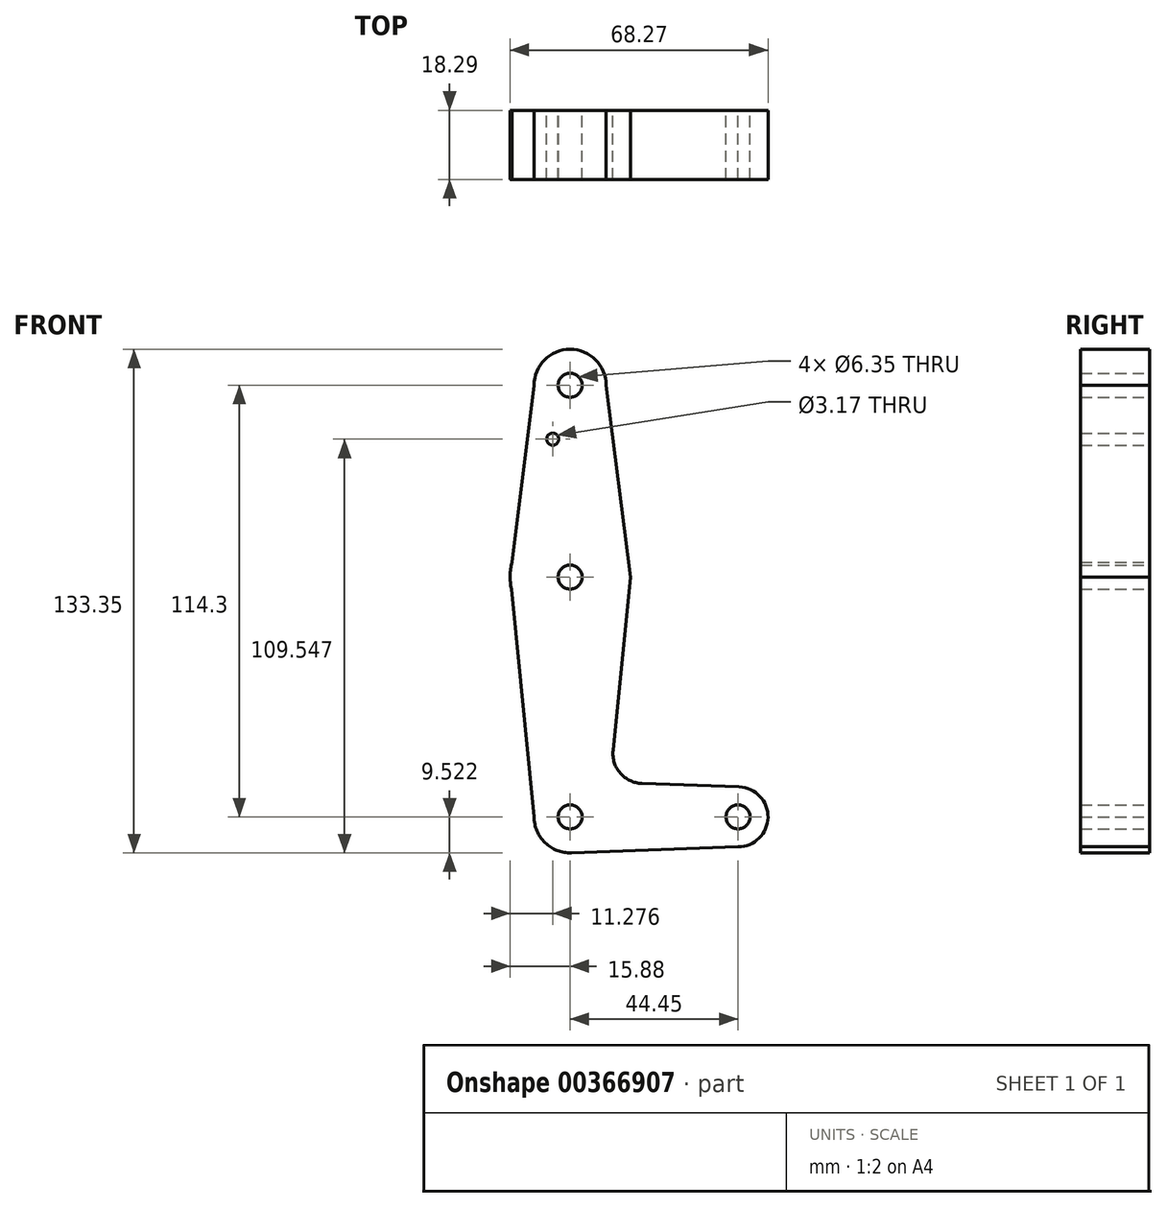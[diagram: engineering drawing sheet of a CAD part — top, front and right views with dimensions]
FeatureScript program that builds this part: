
annotation { "Feature Type Name" : "Feature", "Feature Type Description" : "" }
export const myFeature = defineFeature(function(context is Context, id is Id, definition is map)
    precondition{}
    {
        {
            var Q0;
            Q0=qCreatedBy(makeId("Front.planeOp"),FACE);
            var sketch = newSketch(context, id + "F0", { "sketchPlane" : qUnion([Q0])});
            skCircle(sketch, "E0", {"center": v(0, 88.41) * mm, "radius": 9.53 * mm});
            skCircle(sketch, "E1", {"center": v(0, 37.61) * mm, "radius": 15.88 * mm});
            skCircle(sketch, "E2", {"center": v(0, -25.89) * mm, "radius": 9.53 * mm});
            skCircle(sketch, "E3", {"center": v(44.45, -25.89) * mm, "radius": 7.94 * mm});
            skLineSegment(sketch, "E4", {"start": v(0, 88.41) * mm, "end": v(0, -25.89) * mm});
            skLineSegment(sketch, "E5", {"start": v(44.45, -25.89) * mm, "end": v(0, -25.89) * mm});
            skLineSegment(sketch, "E6", {"start": v(-9.53, 88.41) * mm, "end": v(-15.88, 37.61) * mm});
            skLineSegment(sketch, "E7", {"start": v(-15.88, 37.61) * mm, "end": v(-9.52, -25.89) * mm});
            skLineSegment(sketch, "E8", {"start": v(9.52, 88.41) * mm, "end": v(16, 37.61) * mm});
            skLineSegment(sketch, "E9", {"start": v(16, 37.61) * mm, "end": v(11.36, -8.3) * mm});
            skLineSegment(sketch, "E10", {"start": v(18.98, -17.04) * mm, "end": v(44.73, -17.96) * mm});
            skLineSegment(sketch, "E11", {"start": v(44.45, -33.83) * mm, "end": v(0, -35.42) * mm});
            skCircle(sketch, "E12", {"center": v(0, 88.41) * mm, "radius": 3.18 * mm});
            skCircle(sketch, "E13", {"center": v(0, 37.61) * mm, "radius": 3.17 * mm});
            skCircle(sketch, "E14", {"center": v(0, -25.89) * mm, "radius": 3.18 * mm});
            skCircle(sketch, "E15", {"center": v(44.45, -25.89) * mm, "radius": 3.18 * mm});
            skArc(sketch, "E16.filletArc", {"start": v(11.36, -8.3) * mm, "mid": v(13.27, -14.32) * mm, "end": v(18.98, -17.04) * mm});
            skCircle(sketch, "E17", {"center": v(-4.6, 74.14) * mm, "radius": 1.59 * mm});
            skSolve(sketch);
        }
        {
            var Q0;
            Q0 = qSketchRegion(id + "F0", true);
            var Q1;
            {var subQ0=sQuery(id+"F0.wireOp",EDGE,"E4");var subQ1=sQuery(id+"F0.wireOp",EDGE,"E2");var subQ2=makeQuery(id+"F0.imprint","INTERSECT",VERTEX,{"derivedFrom":[subQ1,subQ0]});Q1=makeQuery(id+"F0.imprint","IMPRINT",FACE,{"disambiguationData":[TD([[makeQuery(id+"F0.imprint","IMPRINT",EDGE,{"disambiguationData":[TD([[subQ2,1.0]])],"derivedFrom":subQ1}),1.0]])]});}
            extrude(context, id + "F1", {"entities" : qUnion([Q0, Q1]), "depth" : 18.29 * mm});
        }
    });
